# Revit family: Hager-Vega-IP40-sistema-PT-pt
name_source: partatom
category: Electrical Equipment
units: mm (PartAtom-declared; Revit-internal decimal feet)

## family parameters
Cut with Voids When Loaded = No
Host = Face
Panel Configuration = Two Columns, Circuits Across
Part Type = Panelboard
Room Calculation Point = No
Round Connector Dimension = Use Diameter
Shared = No

## types (8) — shared parameters
EF000003 - Método de montagem = EV000384 - Montagem em superfície (gesso)
EF000007 - Cor = EV000202 - Branco
EF000008 - Largura = 400 mm  [stored 1.31234 ft]
EF000049 - Profundidade = 146 mm  [stored 0.479003 ft]
EF000116 - Número RAL = 9010
EF000118 - Com tampa de montagem = No
EF000339 - Tipo de difusor = EV004216 - Porta
EF001062 - Versão EMC = No
EF001088 - Extensão possível = Yes
EF001131 - Profundidade interior = 120 mm
EF001134 - Calha DIN = Yes
EF001596 - Material do corpo = EV000139 - Plástico
EF002950 - Largura em número de módulos = 18
EF004462 - Tipo de fecho = EV000154 - Outro
EF005474 - Grau de proteção (IP) = EV006415 - IP40
EF006306 - Com fecho = No
EF009212 - Tipo de tampa = EV000116 - Fechado
EF015776 - Borne de terra = Yes
EF015777 - Borne de neutro = No
EF015941 - Porta para passagem de sinal = Yes
HG000001 - Número de colunas = 1
HG000002 - Com porta ou tampa = Yes
HG000003 - Gama = Vega
HG000005 - Espessura = 3 mm  [stored 0.00984252 ft]
HG000006 - Encastrado = No
HG000009 - Porta dupla = No
HG000010 - Portas assimétricas = No
HG000011 - Filas vazias desde da parte de baixo = No
HG000017 - Distância entre polos = 18 mm  [stored 0.0590551 ft]
Manufacturer = Hager
Type Comments = Vega
zero-valued in all types: Default Elevation, EF000218 - Profundidade incorporada, EF000332 - Altura embutida, EF000846 - Largura para embutir, HG000007 - Número de colunas vazias, HG000008 - Número de filas vazias

## per-type parameters (varying)
| type | EF000040 - Altura | EF000266 - Número de linhas | EF006244 - Tampa/porta transparente | HG000004 - Referência do Fabricante | Model |
| Montagem em superfície IP40 L400 A325 P146 18 unidade de divisão - VB118PP | 325 mm | 1 | No | VB118PP | VB118PP |
| Montagem em superfície IP40 L400 A325 P146 18 unidade de divisão - VB118TP | 325 mm | 1 | Yes | VB118TP | VB118TP |
| Montagem em superfície IP40 L400 A475 P146 18 unidade de divisão - VB218PP | 475 mm  [stored 1.5584 ft] | 2 | No | VB218PP | VB218PP |
| Montagem em superfície IP40 L400 A475 P146 18 unidade de divisão - VB218TP | 475 mm  [stored 1.5584 ft] | 2 | Yes | VB218TP | VB218TP |
| Montagem em superfície IP40 L400 A625 P146 18 unidade de divisão - VB318PP | 625 mm  [stored 2.05052 ft] | 3 | No | VB318PP | VB318PP |
| Montagem em superfície IP40 L400 A625 P146 18 unidade de divisão - VB318TP | 625 mm  [stored 2.05052 ft] | 3 | Yes | VB318TP | VB318TP |
| Montagem em superfície IP40 L400 A775 P146 18 unidade de divisão - VB418PP | 775 mm  [stored 2.54265 ft] | 4 | No | VB418PP | VB418PP |
| Montagem em superfície IP40 L400 A775 P146 18 unidade de divisão - VB418TP | 775 mm  [stored 2.54265 ft] | 4 | Yes | VB418TP | VB418TP |

note: [stored X ft] marks values corroborated as IEEE doubles in the binary element streams (Revit-internal decimal feet)

## geometry (parser evidence)
native form markers: Sweep x17
no freeform markers — native parametric forms only
